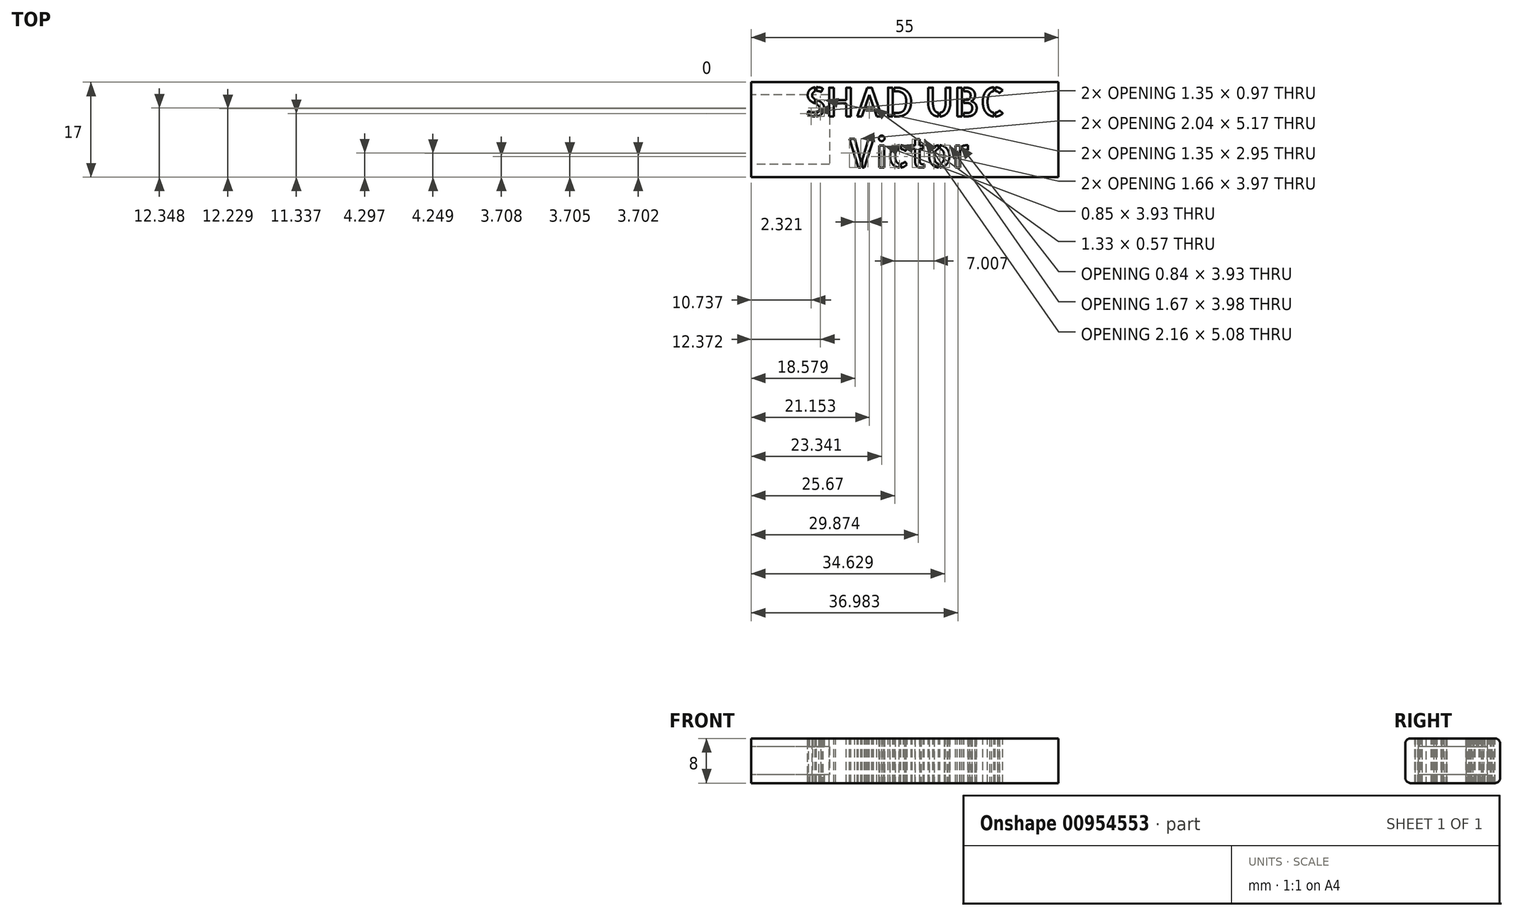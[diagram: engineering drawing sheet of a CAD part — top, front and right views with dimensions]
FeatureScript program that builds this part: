
annotation { "Feature Type Name" : "Feature", "Feature Type Description" : "" }
export const myFeature = defineFeature(function(context is Context, id is Id, definition is map)
    precondition{}
    {
        {
            var Q0;
            Q0=qCreatedBy(makeId("Front.planeOp"),FACE);
            var sketch = newSketch(context, id + "F0", { "sketchPlane" : qUnion([Q0])});
            skLineSegment(sketch, "E0.bottom", {"start": v(-7.5, 4) * mm, "end": v(7.5, 4) * mm});
            skLineSegment(sketch, "E0.top", {"start": v(-7.5, -4) * mm, "end": v(7.5, -4) * mm});
            skLineSegment(sketch, "E0.left", {"start": v(-8.5, 3) * mm, "end": v(-8.5, -3) * mm});
            skLineSegment(sketch, "E0.right", {"start": v(8.5, 3) * mm, "end": v(8.5, -3) * mm});
            skPoint(sketch, "E0.middle", {"position": v(0, 0) * mm});
            skPoint(sketch, "E1.visualSharp", {"position": v(-8.5, 4) * mm});
            skArc(sketch, "E1.filletArc", {"start": v(-7.5, 4) * mm, "mid": v(-8.2, 3.7) * mm, "end": v(-8.5, 3) * mm});
            skPoint(sketch, "E2.visualSharp", {"position": v(8.5, 4) * mm});
            skArc(sketch, "E2.filletArc", {"start": v(8.5, 3) * mm, "mid": v(8.2, 3.7) * mm, "end": v(7.5, 4) * mm});
            skPoint(sketch, "E3.visualSharp", {"position": v(8.5, -4) * mm});
            skArc(sketch, "E3.filletArc", {"start": v(7.5, -4) * mm, "mid": v(8.2, -3.7) * mm, "end": v(8.5, -3) * mm});
            skPoint(sketch, "E4.visualSharp", {"position": v(-8.5, -4) * mm});
            skArc(sketch, "E4.filletArc", {"start": v(-8.5, -3) * mm, "mid": v(-8.2, -3.7) * mm, "end": v(-7.5, -4) * mm});
            skSolve(sketch);
        }
        {
            var Q0;
            Q0=makeQuery(id+"F0.imprint","IMPRINT",FACE,{"disambiguationData":[TD([[makeQuery(id+"F0.imprint","IMPRINT",EDGE,{"derivedFrom":sQuery(id+"F0.wireOp",EDGE,"E0.bottom")}),-1.0]])]});
            extrude(context, id + "F1", {"entities" : qUnion([Q0]), "depth" : 55 * mm, "offsetDistance" : 25 * mm});
        }
        {
            var Q0;
            Q0=makeQuery(id+"F1.opExtrude","CAP_FACE",FACE,{"disambiguationData":[OSD([sQuery(id+"F0.wireOp",EDGE,"E0.bottom"),sQuery(id+"F0.wireOp",EDGE,"E0.top"),sQuery(id+"F0.wireOp",EDGE,"E0.left"),sQuery(id+"F0.wireOp",EDGE,"E0.right"),sQuery(id+"F0.wireOp",EDGE,"E1.filletArc"),sQuery(id+"F0.wireOp",EDGE,"E2.filletArc"),sQuery(id+"F0.wireOp",EDGE,"E3.filletArc"),sQuery(id+"F0.wireOp",EDGE,"E4.filletArc")])],"isStart":false});
            var sketch = newSketch(context, id + "F2", { "sketchPlane" : qUnion([Q0])});
            skLineSegment(sketch, "E5.bottom", {"start": v(-6.2, 2.5) * mm, "end": v(6.2, 2.5) * mm});
            skLineSegment(sketch, "E5.top", {"start": v(-6.2, -2.5) * mm, "end": v(6.2, -2.5) * mm});
            skLineSegment(sketch, "E5.left", {"start": v(-6.2, 2.5) * mm, "end": v(-6.2, -2.5) * mm});
            skLineSegment(sketch, "E5.right", {"start": v(6.2, 2.5) * mm, "end": v(6.2, -2.5) * mm});
            skPoint(sketch, "E5.middle", {"position": v(0, 0) * mm});
            skSolve(sketch);
        }
        {
            var Q0;
            Q0 = qSketchRegion(id + "F2", true);
            extrude(context, id + "F3", {"entities" : qUnion([Q0]), "operationType" : NewBodyOperationType.REMOVE, "oppositeDirection" : true, "depth" : 14 * mm, "offsetDistance" : 25 * mm});
        }
        {
            var Q0;
            Q0=makeQuery(id+"F1.opExtrude","SWEPT_BODY",BODY,{"disambiguationData":[OSD([sQuery(id+"F0.wireOp",EDGE,"E0.bottom"),sQuery(id+"F0.wireOp",EDGE,"E0.top"),sQuery(id+"F0.wireOp",EDGE,"E0.left"),sQuery(id+"F0.wireOp",EDGE,"E0.right"),sQuery(id+"F0.wireOp",EDGE,"E1.filletArc"),sQuery(id+"F0.wireOp",EDGE,"E2.filletArc"),sQuery(id+"F0.wireOp",EDGE,"E3.filletArc"),sQuery(id+"F0.wireOp",EDGE,"E4.filletArc")])]});
            var Q1;
            Q1=makeQuery(id+"F1.opExtrude","CAP_EDGE",EDGE,{"disambiguationData":[OSD([sQuery(id+"F0.wireOp",EDGE,"E0.left")])],"isStart":true});
            transform(context, id + "F4", {"entities" : qUnion([Q0]), "transformType" : TransformType.ROTATION, "transformAxis" : qUnion([Q1]), "angle" : 90 * degree, "makeCopy" : false});
        }
        {
            var Q0;
            Q0=makeQuery(id+"F1.opExtrude","SWEPT_FACE",FACE,{"disambiguationData":[OSD([sQuery(id+"F0.wireOp",EDGE,"E0.bottom")])]});
            var sketch = newSketch(context, id + "F5", { "sketchPlane" : qUnion([Q0])});
            skText(sketch, "E6", { "text": "SHAD UBC\n    Victor", "fontName": "AllertaStencil-Regular.ttf"});
            const initialGuessF5  = {"E6": [-0.054, -0.00612, 1, 0, 0.00514]};
            skSetInitialGuess(sketch, initialGuessF5);
            skSolve(sketch);
        }
        {
            var Q0;
            Q0 = qSketchRegion(id + "F5", true);
            extrude(context, id + "F6", {"entities" : qUnion([Q0]), "operationType" : NewBodyOperationType.REMOVE, "oppositeDirection" : true, "depth" : 12 * mm, "offsetDistance" : 25 * mm});
        }
    });
